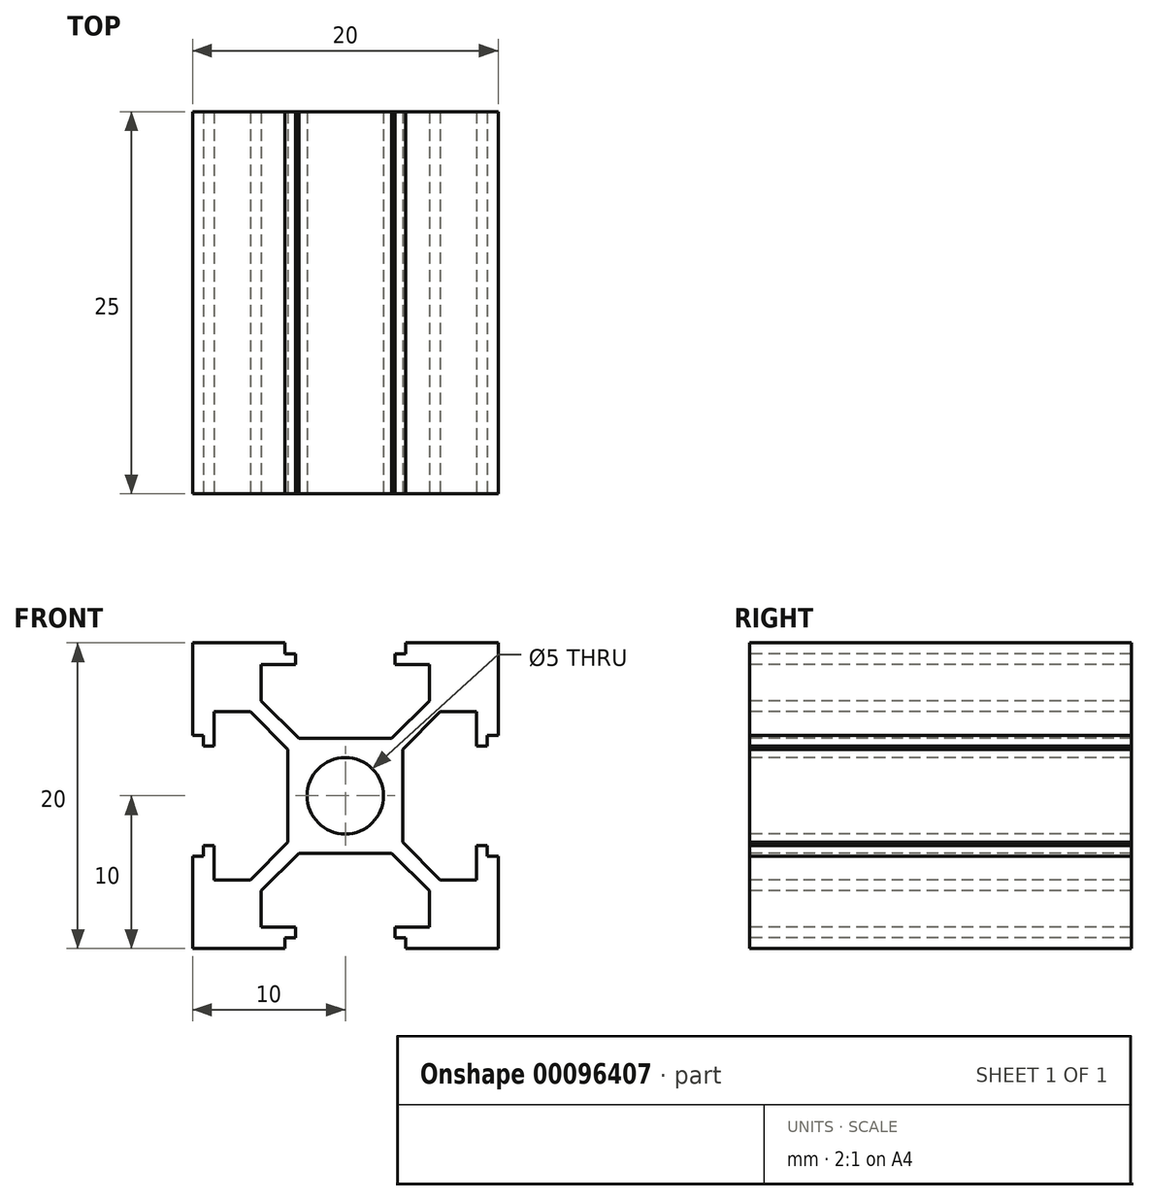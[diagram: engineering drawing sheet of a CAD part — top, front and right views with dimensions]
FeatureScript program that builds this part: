
annotation { "Feature Type Name" : "Feature", "Feature Type Description" : "" }
export const myFeature = defineFeature(function(context is Context, id is Id, definition is map)
    precondition{}
    {
        {
            var Q0;
            Q0=qCreatedBy(makeId("Front.planeOp"),FACE);
            var sketch = newSketch(context, id + "F0", { "sketchPlane" : qUnion([Q0])});
            skLineSegment(sketch, "E0.bottom", {"start": v(0, 0) * mm, "end": v(10, 0) * mm, "construction": true});
            skLineSegment(sketch, "E0.top", {"start": v(0, 10) * mm, "end": v(10, 10) * mm, "construction": true});
            skLineSegment(sketch, "E0.left", {"start": v(0, 0) * mm, "end": v(0, 10) * mm, "construction": true});
            skLineSegment(sketch, "E0.right", {"start": v(10, 0) * mm, "end": v(10, 10) * mm, "construction": true});
            skLineSegment(sketch, "E1", {"start": v(10, 10) * mm, "end": v(0, 0) * mm, "construction": true});
            skLineSegment(sketch, "E2", {"start": v(10, 10) * mm, "end": v(10, 3.95) * mm});
            skLineSegment(sketch, "E3", {"start": v(10, 3.95) * mm, "end": v(9.3, 3.95) * mm});
            skLineSegment(sketch, "E4", {"start": v(9.3, 3.95) * mm, "end": v(9.3, 3.25) * mm});
            skLineSegment(sketch, "E5", {"start": v(9.3, 3.25) * mm, "end": v(8.6, 3.25) * mm});
            skLineSegment(sketch, "E6", {"start": v(8.6, 3.25) * mm, "end": v(8.6, 5.5) * mm});
            skLineSegment(sketch, "E7", {"start": v(8.6, 5.5) * mm, "end": v(6.2, 5.5) * mm});
            skLineSegment(sketch, "E8", {"start": v(6.2, 5.5) * mm, "end": v(3.75, 3.04) * mm});
            skLineSegment(sketch, "E9", {"start": v(3.75, 3.04) * mm, "end": v(3.75, 0) * mm});
            skLineSegment(sketch, "E10.MirrorCS", {"start": v(10, 10) * mm, "end": v(3.95, 10) * mm});
            skLineSegment(sketch, "E11.MirrorCS", {"start": v(3.95, 9.3) * mm, "end": v(3.25, 9.3) * mm});
            skLineSegment(sketch, "E12.MirrorCS", {"start": v(3.95, 10) * mm, "end": v(3.95, 9.3) * mm});
            skLineSegment(sketch, "E13.MirrorCS", {"start": v(3.25, 9.3) * mm, "end": v(3.25, 8.6) * mm});
            skLineSegment(sketch, "E14.MirrorCS", {"start": v(3.04, 3.75) * mm, "end": v(0, 3.75) * mm});
            skLineSegment(sketch, "E15.MirrorCS", {"start": v(5.5, 6.2) * mm, "end": v(3.04, 3.75) * mm});
            skLineSegment(sketch, "E16.MirrorCS", {"start": v(5.5, 8.6) * mm, "end": v(5.5, 6.2) * mm});
            skLineSegment(sketch, "E17.MirrorCS", {"start": v(3.25, 8.6) * mm, "end": v(5.5, 8.6) * mm});
            skLineSegment(sketch, "E18.1.0", {"start": v(0, 0) * mm, "end": v(-10, 0) * mm, "construction": true});
            skLineSegment(sketch, "E18.1.1", {"start": v(-3.04, 3.75) * mm, "end": v(0, 3.75) * mm});
            skLineSegment(sketch, "E18.1.2", {"start": v(-10, 0) * mm, "end": v(-10, 10) * mm, "construction": true});
            skLineSegment(sketch, "E18.1.3", {"start": v(-5.5, 8.6) * mm, "end": v(-5.5, 6.2) * mm});
            skLineSegment(sketch, "E18.1.5", {"start": v(-10, 10) * mm, "end": v(0, 0) * mm, "construction": true});
            skLineSegment(sketch, "E18.1.6", {"start": v(-10, 10) * mm, "end": v(-3.95, 10) * mm});
            skLineSegment(sketch, "E18.1.7", {"start": v(-3.25, 8.6) * mm, "end": v(-5.5, 8.6) * mm});
            skLineSegment(sketch, "E18.1.8", {"start": v(-5.5, 6.2) * mm, "end": v(-3.04, 3.75) * mm});
            skLineSegment(sketch, "E18.1.9", {"start": v(-8.6, 3.25) * mm, "end": v(-8.6, 5.5) * mm});
            skLineSegment(sketch, "E18.1.10", {"start": v(-6.2, 5.5) * mm, "end": v(-3.75, 3.04) * mm});
            skLineSegment(sketch, "E18.1.11", {"start": v(-3.75, 3.04) * mm, "end": v(-3.75, 0) * mm});
            skLineSegment(sketch, "E18.1.12", {"start": v(0, 10) * mm, "end": v(-10, 10) * mm, "construction": true});
            skLineSegment(sketch, "E18.1.13", {"start": v(-10, 10) * mm, "end": v(-10, 3.95) * mm});
            skLineSegment(sketch, "E18.1.14", {"start": v(-8.6, 5.5) * mm, "end": v(-6.2, 5.5) * mm});
            skLineSegment(sketch, "E18.1.15", {"start": v(-3.95, 10) * mm, "end": v(-3.95, 9.3) * mm});
            skLineSegment(sketch, "E18.1.16", {"start": v(-3.95, 9.3) * mm, "end": v(-3.25, 9.3) * mm});
            skLineSegment(sketch, "E18.1.17", {"start": v(-3.25, 9.3) * mm, "end": v(-3.25, 8.6) * mm});
            skLineSegment(sketch, "E18.1.18", {"start": v(-9.3, 3.95) * mm, "end": v(-9.3, 3.25) * mm});
            skLineSegment(sketch, "E18.1.19", {"start": v(-10, 3.95) * mm, "end": v(-9.3, 3.95) * mm});
            skLineSegment(sketch, "E18.1.20", {"start": v(-9.3, 3.25) * mm, "end": v(-8.6, 3.25) * mm});
            skLineSegment(sketch, "E18.2.0", {"start": v(0, 0) * mm, "end": v(0, -10) * mm, "construction": true});
            skLineSegment(sketch, "E18.2.1", {"start": v(-3.75, -3.04) * mm, "end": v(-3.75, 0) * mm});
            skLineSegment(sketch, "E18.2.2", {"start": v(0, -10) * mm, "end": v(-10, -10) * mm, "construction": true});
            skLineSegment(sketch, "E18.2.3", {"start": v(-8.6, -5.5) * mm, "end": v(-6.2, -5.5) * mm});
            skLineSegment(sketch, "E18.2.4", {"start": v(0, 0) * mm, "end": v(-10, 0) * mm, "construction": true});
            skLineSegment(sketch, "E18.2.5", {"start": v(-10, -10) * mm, "end": v(0, 0) * mm, "construction": true});
            skLineSegment(sketch, "E18.2.6", {"start": v(-10, -10) * mm, "end": v(-10, -3.95) * mm});
            skLineSegment(sketch, "E18.2.7", {"start": v(-8.6, -3.25) * mm, "end": v(-8.6, -5.5) * mm});
            skLineSegment(sketch, "E18.2.8", {"start": v(-6.2, -5.5) * mm, "end": v(-3.75, -3.04) * mm});
            skLineSegment(sketch, "E18.2.9", {"start": v(-3.25, -8.6) * mm, "end": v(-5.5, -8.6) * mm});
            skLineSegment(sketch, "E18.2.10", {"start": v(-5.5, -6.2) * mm, "end": v(-3.04, -3.75) * mm});
            skLineSegment(sketch, "E18.2.11", {"start": v(-3.04, -3.75) * mm, "end": v(0, -3.75) * mm});
            skLineSegment(sketch, "E18.2.12", {"start": v(-10, 0) * mm, "end": v(-10, -10) * mm, "construction": true});
            skLineSegment(sketch, "E18.2.13", {"start": v(-10, -10) * mm, "end": v(-3.95, -10) * mm});
            skLineSegment(sketch, "E18.2.14", {"start": v(-5.5, -8.6) * mm, "end": v(-5.5, -6.2) * mm});
            skLineSegment(sketch, "E18.2.15", {"start": v(-10, -3.95) * mm, "end": v(-9.3, -3.95) * mm});
            skLineSegment(sketch, "E18.2.16", {"start": v(-9.3, -3.95) * mm, "end": v(-9.3, -3.25) * mm});
            skLineSegment(sketch, "E18.2.17", {"start": v(-9.3, -3.25) * mm, "end": v(-8.6, -3.25) * mm});
            skLineSegment(sketch, "E18.2.18", {"start": v(-3.95, -9.3) * mm, "end": v(-3.25, -9.3) * mm});
            skLineSegment(sketch, "E18.2.19", {"start": v(-3.95, -10) * mm, "end": v(-3.95, -9.3) * mm});
            skLineSegment(sketch, "E18.2.20", {"start": v(-3.25, -9.3) * mm, "end": v(-3.25, -8.6) * mm});
            skLineSegment(sketch, "E18.3.1", {"start": v(3.04, -3.75) * mm, "end": v(0, -3.75) * mm});
            skLineSegment(sketch, "E18.3.2", {"start": v(10, 0) * mm, "end": v(10, -10) * mm, "construction": true});
            skLineSegment(sketch, "E18.3.3", {"start": v(5.5, -8.6) * mm, "end": v(5.5, -6.2) * mm});
            skLineSegment(sketch, "E18.3.4", {"start": v(0, 0) * mm, "end": v(0, -10) * mm, "construction": true});
            skLineSegment(sketch, "E18.3.5", {"start": v(10, -10) * mm, "end": v(0, 0) * mm, "construction": true});
            skLineSegment(sketch, "E18.3.6", {"start": v(10, -10) * mm, "end": v(3.95, -10) * mm});
            skLineSegment(sketch, "E18.3.7", {"start": v(3.25, -8.6) * mm, "end": v(5.5, -8.6) * mm});
            skLineSegment(sketch, "E18.3.8", {"start": v(5.5, -6.2) * mm, "end": v(3.04, -3.75) * mm});
            skLineSegment(sketch, "E18.3.9", {"start": v(8.6, -3.25) * mm, "end": v(8.6, -5.5) * mm});
            skLineSegment(sketch, "E18.3.10", {"start": v(6.2, -5.5) * mm, "end": v(3.75, -3.04) * mm});
            skLineSegment(sketch, "E18.3.11", {"start": v(3.75, -3.04) * mm, "end": v(3.75, 0) * mm});
            skLineSegment(sketch, "E18.3.12", {"start": v(0, -10) * mm, "end": v(10, -10) * mm, "construction": true});
            skLineSegment(sketch, "E18.3.13", {"start": v(10, -10) * mm, "end": v(10, -3.95) * mm});
            skLineSegment(sketch, "E18.3.14", {"start": v(8.6, -5.5) * mm, "end": v(6.2, -5.5) * mm});
            skLineSegment(sketch, "E18.3.15", {"start": v(3.95, -10) * mm, "end": v(3.95, -9.3) * mm});
            skLineSegment(sketch, "E18.3.16", {"start": v(3.95, -9.3) * mm, "end": v(3.25, -9.3) * mm});
            skLineSegment(sketch, "E18.3.17", {"start": v(3.25, -9.3) * mm, "end": v(3.25, -8.6) * mm});
            skLineSegment(sketch, "E18.3.18", {"start": v(9.3, -3.95) * mm, "end": v(9.3, -3.25) * mm});
            skLineSegment(sketch, "E18.3.19", {"start": v(10, -3.95) * mm, "end": v(9.3, -3.95) * mm});
            skLineSegment(sketch, "E18.3.20", {"start": v(9.3, -3.25) * mm, "end": v(8.6, -3.25) * mm});
            skPoint(sketch, "E18.center", {"position": v(0, 0) * mm});
            skCircle(sketch, "E19", {"center": v(0, 0) * mm, "radius": 2.5 * mm});
            skSolve(sketch);
        }
        {
            var Q0;
            Q0=makeQuery(id+"F0.imprint","IMPRINT",FACE,{"disambiguationData":[TD([[makeQuery(id+"F0.imprint","IMPRINT",EDGE,{"derivedFrom":sQuery(id+"F0.wireOp",EDGE,"E2")}),-1.0]])]});
            extrude(context, id + "F1", {"entities" : qUnion([Q0]), "oppositeDirection" : true, "depth" : 25 * mm});
        }
    });
